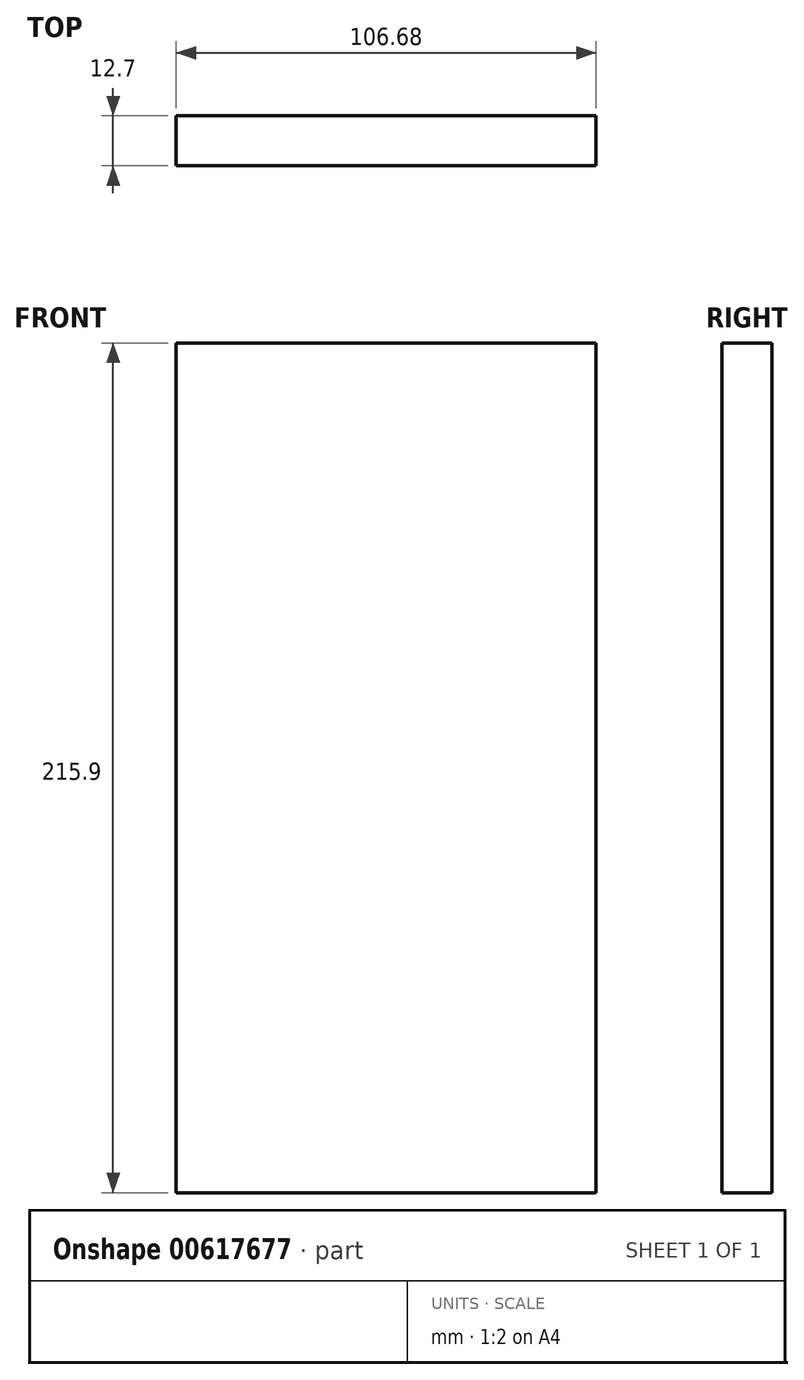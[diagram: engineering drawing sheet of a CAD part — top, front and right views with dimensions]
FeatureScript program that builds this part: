
annotation { "Feature Type Name" : "Feature", "Feature Type Description" : "" }
export const myFeature = defineFeature(function(context is Context, id is Id, definition is map)
    precondition{}
    {
        {
            var Q0;
            Q0=qCreatedBy(makeId("Front.planeOp"),FACE);
            var sketch = newSketch(context, id + "F0", { "sketchPlane" : qUnion([Q0])});
            skLineSegment(sketch, "E0.bottom", {"start": v(-11.04, -10.54) * mm, "end": v(-117.72, -10.54) * mm});
            skLineSegment(sketch, "E0.top", {"start": v(-11.04, 205.36) * mm, "end": v(-117.72, 205.36) * mm});
            skLineSegment(sketch, "E0.left", {"start": v(-11.04, -10.54) * mm, "end": v(-11.04, 205.36) * mm});
            skLineSegment(sketch, "E0.right", {"start": v(-117.72, -10.54) * mm, "end": v(-117.72, 205.36) * mm});
            skPoint(sketch, "E0.middle", {"position": v(-64.38, 97.41) * mm});
            skSolve(sketch);
        }
        {
            var Q0;
            Q0 = qSketchRegion(id + "F0", true);
            extrude(context, id + "F1", {"entities" : qUnion([Q0]), "endBound" : BoundingType.SYMMETRIC, "depth" : 12.7 * mm, "offsetDistance" : 25.4 * mm});
        }
    });
